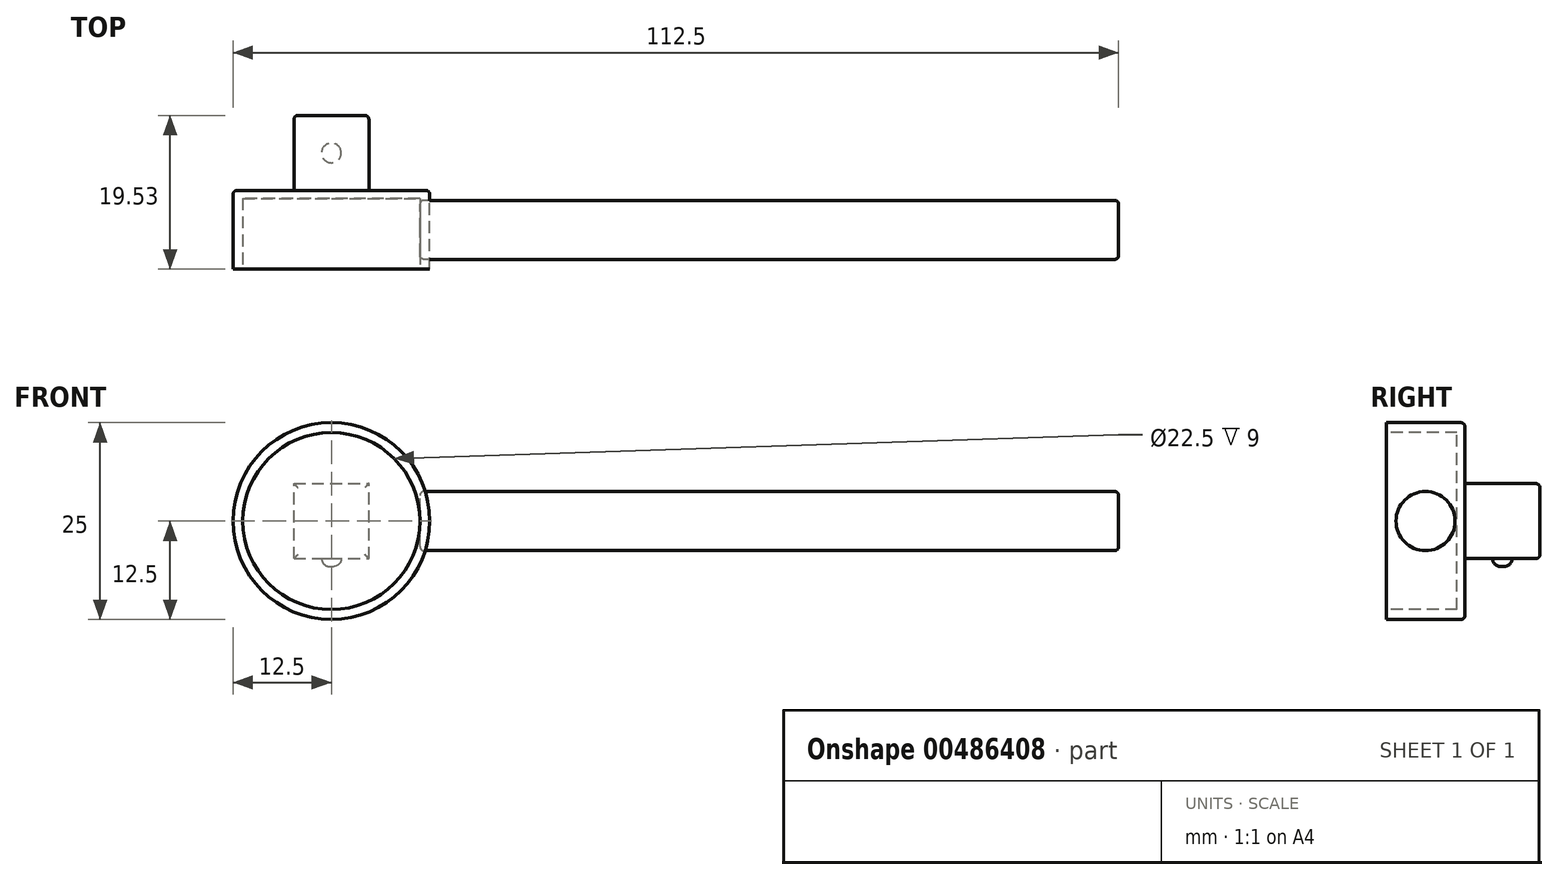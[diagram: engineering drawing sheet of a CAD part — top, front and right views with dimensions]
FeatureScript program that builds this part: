
annotation { "Feature Type Name" : "Feature", "Feature Type Description" : "" }
export const myFeature = defineFeature(function(context is Context, id is Id, definition is map)
    precondition{}
    {
        {
            var Q0;
            Q0=qCreatedBy(makeId("Front.planeOp"),FACE);
            var sketch = newSketch(context, id + "F0", { "sketchPlane" : qUnion([Q0])});
            skCircle(sketch, "E0", {"center": v(0, 0) * mm, "radius": 12.5 * mm});
            skSolve(sketch);
        }
        {
            var Q0;
            Q0 = qSketchRegion(id + "F0", true);
            extrude(context, id + "F1", {"entities" : qUnion([Q0]), "depth" : 10 * mm});
        }
        {
            var Q0;
            Q0=makeQuery(id+"F1.opExtrude","CAP_FACE",FACE,{"disambiguationData":[OSD([sQuery(id+"F0.wireOp",EDGE,"E0")])],"isStart":false});
            var sketch = newSketch(context, id + "F2", { "sketchPlane" : qUnion([Q0])});
            skCircle(sketch, "E1", {"center": v(0, 0) * mm, "radius": 11.25 * mm});
            skSolve(sketch);
        }
        {
            var Q0;
            Q0 = qSketchRegion(id + "F2", true);
            extrude(context, id + "F3", {"entities" : qUnion([Q0]), "operationType" : NewBodyOperationType.REMOVE, "oppositeDirection" : true, "depth" : 9 * mm});
        }
        {
            var Q0;
            Q0=makeQuery(id+"F1.opExtrude","CAP_FACE",FACE,{"disambiguationData":[OSD([sQuery(id+"F0.wireOp",EDGE,"E0")])],"isStart":true});
            var sketch = newSketch(context, id + "F4", { "sketchPlane" : qUnion([Q0])});
            skLineSegment(sketch, "E2.bottom", {"start": v(4.76, -4.76) * mm, "end": v(-4.76, -4.76) * mm});
            skLineSegment(sketch, "E2.top", {"start": v(4.76, 4.76) * mm, "end": v(-4.76, 4.76) * mm});
            skLineSegment(sketch, "E2.left", {"start": v(4.76, -4.76) * mm, "end": v(4.76, 4.76) * mm});
            skLineSegment(sketch, "E2.right", {"start": v(-4.76, -4.76) * mm, "end": v(-4.76, 4.76) * mm});
            skPoint(sketch, "E2.middle", {"position": v(0, 0) * mm});
            skSolve(sketch);
        }
        {
            var Q0;
            Q0 = qSketchRegion(id + "F4", true);
            extrude(context, id + "F5", {"entities" : qUnion([Q0]), "operationType" : NewBodyOperationType.ADD, "depth" : 9.53 * mm});
        }
        {
            var Q0;
            Q0=qCreatedBy(makeId("Right.planeOp"),FACE);
            var sketch = newSketch(context, id + "F6", { "sketchPlane" : qUnion([Q0])});
            skCircle(sketch, "E3", {"center": v(-5, 0) * mm, "radius": 3.75 * mm});
            skSolve(sketch);
        }
        {
            var Q0;
            Q0 = qSketchRegion(id + "F6", true);
            extrude(context, id + "F7", {"entities" : qUnion([Q0]), "depth" : 100 * mm, "hasSecondDirection" : true, "secondDirectionOppositeDirection" : false, "secondDirectionDepth" : 11.25 * mm});
        }
        {
            var Q0;
            Q0=makeQuery(id+"F5.opExtrude","SWEPT_FACE",FACE,{"disambiguationData":[OSD([sQuery(id+"F4.wireOp",EDGE,"E2.bottom")])]});
            var sketch = newSketch(context, id + "F8", { "sketchPlane" : qUnion([Q0])});
            skCircle(sketch, "E4", {"center": v(0, -4.76) * mm, "radius": 1.25 * mm});
            skPoint(sketch, "E4.centerSnap0", {"position": v(4.76, -4.76) * mm});
            skSolve(sketch);
        }
        {
            var Q0;
            Q0 = qSketchRegion(id + "F8", true);
            extrude(context, id + "F9", {"entities" : qUnion([Q0]), "operationType" : NewBodyOperationType.ADD, "depth" : 1 * mm});
        }
        {
            var Q0;
            Q0=makeQuery(id+"F9.opExtrude","CAP_EDGE",EDGE,{"disambiguationData":[OSD([sQuery(id+"F8.wireOp",EDGE,"E4")])],"isStart":false});
            fillet(context, id + "F10", {"entities" : qUnion([Q0]), "radius" : 1 * mm, "tangentPropagation" : true, "allowEdgeOverflow" : false});
        }
        {
            var Q0;
            Q0=makeQuery(id+"F5.opExtrude","CAP_FACE",FACE,{"disambiguationData":[OSD([sQuery(id+"F4.wireOp",EDGE,"E2.bottom"),sQuery(id+"F4.wireOp",EDGE,"E2.top"),sQuery(id+"F4.wireOp",EDGE,"E2.left"),sQuery(id+"F4.wireOp",EDGE,"E2.right")])],"isStart":false});
            var Q1;
            Q1=makeQuery(id+"F7.opExtrude","SWEPT_FACE",FACE,{"disambiguationData":[OSD([sQuery(id+"F6.wireOp",EDGE,"E3")])]});
            var Q2;
            Q2=makeQuery(id+"F3.boolean.opBoolean","COPY",EDGE,{"derivedFrom":makeQuery(id+"F3.opExtrude","CAP_EDGE",EDGE,{"disambiguationData":[OSD([sQuery(id+"F2.wireOp",EDGE,"E1")])],"isStart":true})});
            var Q3;
            Q3=makeQuery(id+"F1.opExtrude","CAP_EDGE",EDGE,{"disambiguationData":[OSD([sQuery(id+"F0.wireOp",EDGE,"E0")])],"isStart":true});
            fillet(context, id + "F11", {"entities" : qUnion([Q0, Q1, Q2, Q3]), "radius" : 0.5 * mm, "tangentPropagation" : true, "allowEdgeOverflow" : false});
        }
    });
